# Revit family: Rough_Valve-DXV-D350007X0.191
name_source: partatom
category: Plumbing Fixtures
revit_build: Autodesk Revit 2014 (Build: 20130308_1515(x64)
units: mm (PartAtom-declared; Revit-internal decimal feet)

## types (2) — shared parameters
Assembly Code = D2010710
CW Connection = Yes
Default Elevation = 40"
Finish = Brass-DXV-Cast
HW Connection = Yes
Hot Water Connection Diameter = 1"
Installation Type = Wall Mounted
Length = 1 3/4"
Manufacturer = DXV
Material = Brass-DXV-Cast
Price = Prices may vary. Please consult Manufacturer Representative for most up-to-date price list.
Product Documentation Link = https://dxv01.blob.core.windows.net
Product Page URL = https://www.dxv.com
URL = http://www.dxv.com
Vent Connection = No
Warranty Documentation Link = https://www.dxv.com
Waste Connection = No
Width = 1"
zero-valued in all types: CWFU, HWFU, WFU

## per-type parameters (varying)
| type | 1/2" Valve | 3/4" Valve | Cold Water Connection Diameter | Cold Water Connection Radius | Description | Height | Hot Water Connection Radius | Inlet Connection Description | Outlet Connection Description | Tempered Water Connection Diameter | Tempered Water Connection Radius |
| D35000710.191 | Yes | No | 1/2" | 1/4" | 1/2'' Wall Rough Valve | 2 3/8" | 1/4" | 1/2'' NPT Supply Inlet | 1/2'' NPT Supply Outlet | 1/2" | 1/4" |
| D35000700.191 | No | Yes | 3/4" | 3/8" | 3/4'' Wall Rough Valve | 3" | 3/8" | 3/4'' NPT Supply Inlet | 3/4'' NPT Supply Outlet | 3/4" | 3/8" |

note: column(s) folded — value = type name in every type: Model

## geometry (parser evidence)
native form markers: Sweep x3
no freeform markers — native parametric forms only
